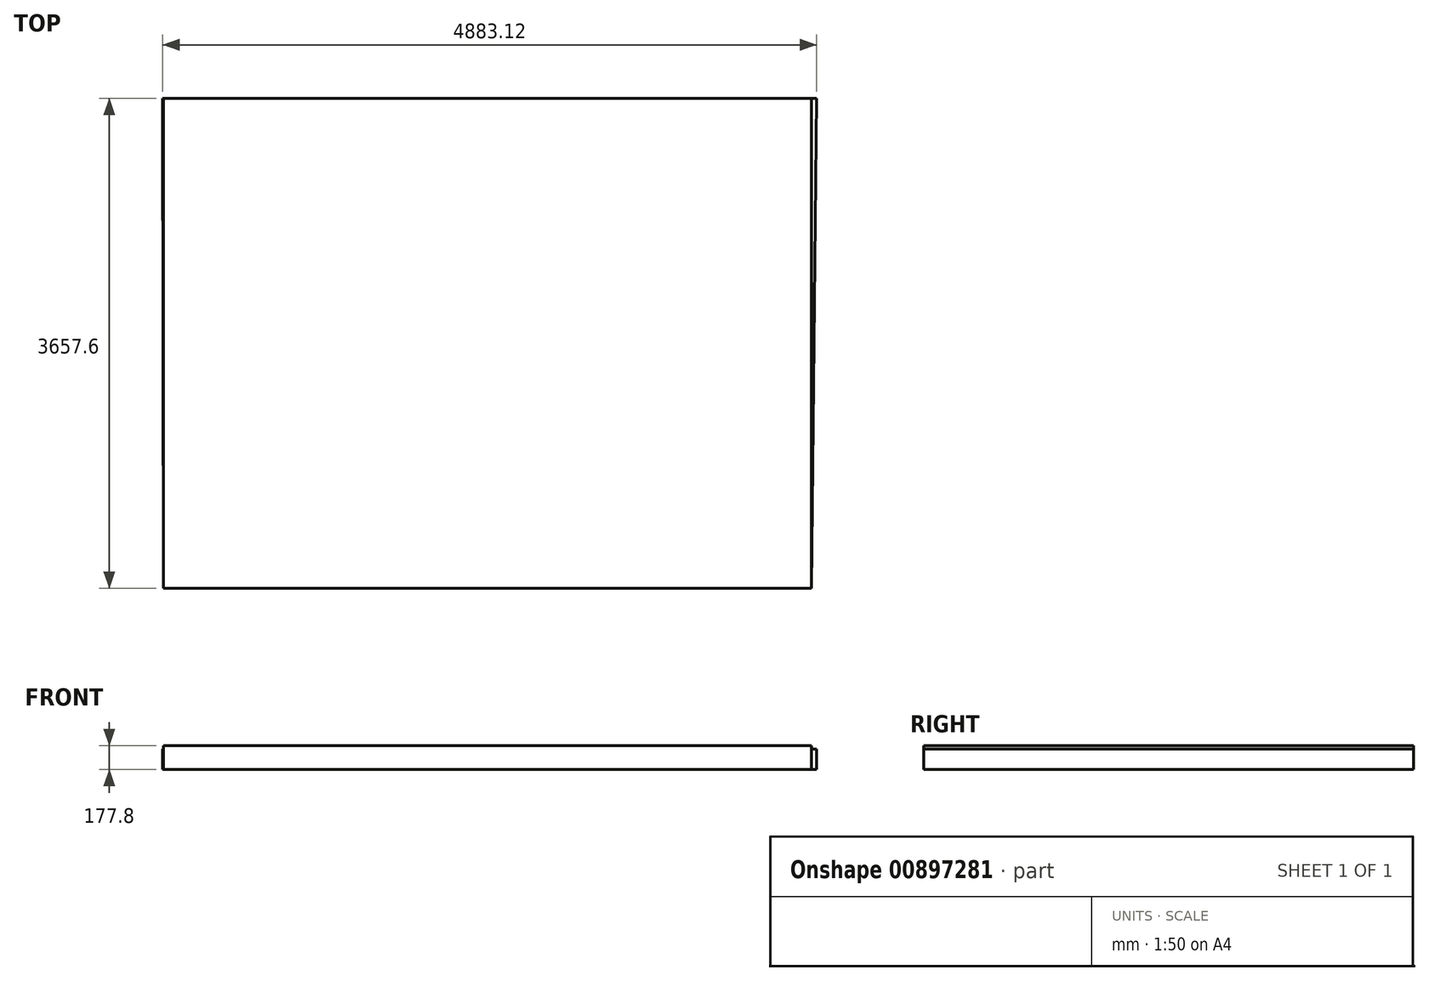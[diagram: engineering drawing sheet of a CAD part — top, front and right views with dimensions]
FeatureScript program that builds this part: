
annotation { "Feature Type Name" : "Feature", "Feature Type Description" : "" }
export const myFeature = defineFeature(function(context is Context, id is Id, definition is map)
    precondition{}
    {
        {
            var Q0;
            Q0=qCreatedBy(makeId("Top.planeOp"),FACE);
            var sketch = newSketch(context, id + "F0", { "sketchPlane" : qUnion([Q0])});
            skLineSegment(sketch, "E0", {"start": v(0, 0) * mm, "end": v(4838.7, 0) * mm});
            skLineSegment(sketch, "E1", {"start": v(4838.7, 0) * mm, "end": v(4876.8, 3657.6) * mm});
            skLineSegment(sketch, "E2", {"start": v(4876.8, 3657.6) * mm, "end": v(-6.32, 3657.6) * mm});
            skLineSegment(sketch, "E3", {"start": v(-6.32, 3657.6) * mm, "end": v(0, 0) * mm});
            skLineSegment(sketch, "E4", {"start": v(4876.8, 3657.6) * mm, "end": v(0, 0) * mm, "construction": true});
            skLineSegment(sketch, "E5", {"start": v(-6.32, 3657.6) * mm, "end": v(4838.7, 0) * mm, "construction": true});
            skSolve(sketch);
        }
        {
            var Q0;
            Q0 = qSketchRegion(id + "F0", true);
            extrude(context, id + "F1", {"entities" : qUnion([Q0]), "oppositeDirection" : true, "depth" : 152.4 * mm, "offsetDistance" : 25.4 * mm});
        }
        {
            var Q0;
            Q0=qCreatedBy(makeId("Top.planeOp"),FACE);
            var sketch = newSketch(context, id + "F2", { "sketchPlane" : qUnion([Q0])});
            skLineSegment(sketch, "E6", {"start": v(0, 0) * mm, "end": v(4838.7, 0) * mm});
            skLineSegment(sketch, "E7", {"start": v(4838.7, 0) * mm, "end": v(4838.7, 3657.6) * mm});
            skLineSegment(sketch, "E8", {"start": v(4838.7, 3657.6) * mm, "end": v(0, 3657.6) * mm});
            skLineSegment(sketch, "E9", {"start": v(0, 3657.6) * mm, "end": v(0, 0) * mm});
            skSolve(sketch);
        }
        {
            var Q0;
            Q0 = qSketchRegion(id + "F2", true);
            extrude(context, id + "F3", {"entities" : qUnion([Q0]), "operationType" : NewBodyOperationType.ADD, "depth" : 25.4 * mm, "offsetDistance" : 25.4 * mm});
        }
    });
